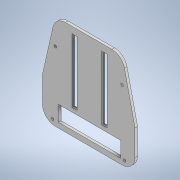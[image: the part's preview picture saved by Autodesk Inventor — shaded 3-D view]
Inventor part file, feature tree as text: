
AUTODESK INVENTOR PART (.ipt)
format: ipt  version: 2020 (Build 240168000, 168)  size: 129,536 bytes
history: native  units: in
note: dims shown in document units (in); Inventor stores cm internally (conversion verified against a paired STEP export)
features: extrude x1, fillet x1, sketch x1
ambient origin geometry x8: Origin, YZ Plane, XZ Plane, XY Plane, X Axis, Y Axis, Z Axis, Center Point
bodies: Solid1 (feature_tree)
feature tree (3):
  extrude  "Extrusion1"  Depth=0.9843in
  fillet  "Fillet1"  [1 undecoded]
  sketch  "Sketch1"  dims[d6=0.1969in d7=0.0in d8=0.9843in]
note: 1 required parameter value undecoded (feature->parameter linkage not recoverable at this tier; creation-order binding heuristic only, values carry confidence <= 0.55)
